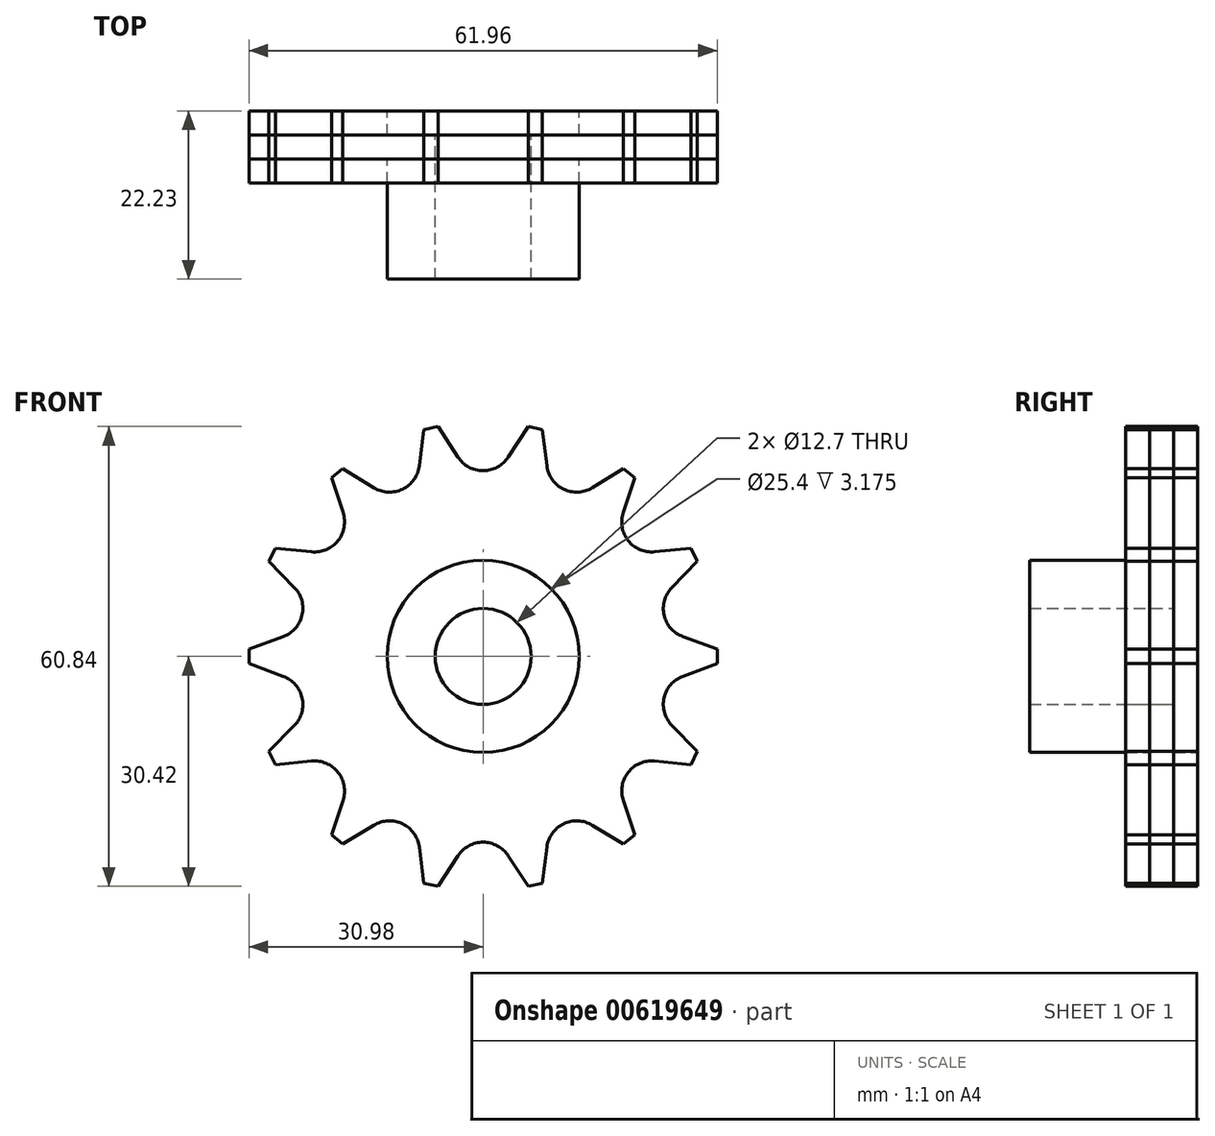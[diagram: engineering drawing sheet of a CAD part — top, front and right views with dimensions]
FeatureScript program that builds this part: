
annotation { "Feature Type Name" : "Feature", "Feature Type Description" : "" }
export const myFeature = defineFeature(function(context is Context, id is Id, definition is map)
    precondition{}
    {
        {
            var Q0;
            Q0=qCreatedBy(makeId("Front.planeOp"),FACE);
            var sketch = newSketch(context, id + "F0", { "sketchPlane" : qUnion([Q0])});
            skCircle(sketch, "E0", {"center": v(0, 0) * mm, "radius": 6.35 * mm});
            skCircle(sketch, "E1", {"center": v(0, 0) * mm, "radius": 12.7 * mm});
            skCircle(sketch, "E2", {"center": v(0, 0) * mm, "radius": 31.26 * mm, "construction": true});
            skLineSegment(sketch, "E3", {"start": v(0, 28.54) * mm, "end": v(0, 0) * mm, "construction": true});
            skLineSegment(sketch, "E4", {"start": v(0, 0) * mm, "end": v(38.17, 0) * mm, "construction": true});
            skLineSegment(sketch, "E5.1.0", {"start": v(-12.38, 25.71) * mm, "end": v(0, 0) * mm, "construction": true});
            skLineSegment(sketch, "E5.2.0", {"start": v(-22.31, 17.8) * mm, "end": v(0, 0) * mm, "construction": true});
            skLineSegment(sketch, "E5.3.0", {"start": v(-27.82, 6.35) * mm, "end": v(0, 0) * mm, "construction": true});
            skLineSegment(sketch, "E5.4.0", {"start": v(-27.82, -6.35) * mm, "end": v(0, 0) * mm, "construction": true});
            skLineSegment(sketch, "E5.5.0", {"start": v(-22.31, -17.8) * mm, "end": v(0, 0) * mm, "construction": true});
            skLineSegment(sketch, "E5.6.0", {"start": v(-12.38, -25.71) * mm, "end": v(0, 0) * mm, "construction": true});
            skLineSegment(sketch, "E5.7.0", {"start": v(0, -28.54) * mm, "end": v(0, 0) * mm, "construction": true});
            skLineSegment(sketch, "E5.8.0", {"start": v(12.38, -25.71) * mm, "end": v(0, 0) * mm, "construction": true});
            skLineSegment(sketch, "E5.9.0", {"start": v(22.31, -17.8) * mm, "end": v(0, 0) * mm, "construction": true});
            skLineSegment(sketch, "E5.10.0", {"start": v(27.82, -6.35) * mm, "end": v(0, 0) * mm, "construction": true});
            skLineSegment(sketch, "E5.11.0", {"start": v(27.82, 6.35) * mm, "end": v(0, 0) * mm, "construction": true});
            skLineSegment(sketch, "E5.12.0", {"start": v(22.31, 17.8) * mm, "end": v(0, 0) * mm, "construction": true});
            skLineSegment(sketch, "E5.13.0", {"start": v(12.38, 25.71) * mm, "end": v(0, 0) * mm, "construction": true});
            skCircle(sketch, "E6", {"center": v(0, 28.54) * mm, "radius": 3.97 * mm, "construction": true});
            skCircle(sketch, "E7.1.0", {"center": v(-12.38, 25.71) * mm, "radius": 3.97 * mm, "construction": true});
            skCircle(sketch, "E7.2.0", {"center": v(-22.31, 17.8) * mm, "radius": 3.97 * mm, "construction": true});
            skCircle(sketch, "E7.3.0", {"center": v(-27.82, 6.35) * mm, "radius": 3.97 * mm, "construction": true});
            skCircle(sketch, "E7.4.0", {"center": v(-27.82, -6.35) * mm, "radius": 3.97 * mm, "construction": true});
            skCircle(sketch, "E7.5.0", {"center": v(-22.31, -17.8) * mm, "radius": 3.97 * mm, "construction": true});
            skCircle(sketch, "E7.6.0", {"center": v(-12.38, -25.71) * mm, "radius": 3.97 * mm, "construction": true});
            skCircle(sketch, "E7.7.0", {"center": v(0, -28.54) * mm, "radius": 3.97 * mm, "construction": true});
            skCircle(sketch, "E7.8.0", {"center": v(12.38, -25.71) * mm, "radius": 3.97 * mm, "construction": true});
            skCircle(sketch, "E7.9.0", {"center": v(22.31, -17.8) * mm, "radius": 3.97 * mm, "construction": true});
            skCircle(sketch, "E7.10.0", {"center": v(27.82, -6.35) * mm, "radius": 3.97 * mm, "construction": true});
            skCircle(sketch, "E7.11.0", {"center": v(27.82, 6.35) * mm, "radius": 3.97 * mm, "construction": true});
            skCircle(sketch, "E7.12.0", {"center": v(22.31, 17.8) * mm, "radius": 3.97 * mm, "construction": true});
            skCircle(sketch, "E7.13.0", {"center": v(12.38, 25.71) * mm, "radius": 3.97 * mm, "construction": true});
            skLineSegment(sketch, "E8", {"start": v(0, 28.54) * mm, "end": v(12.38, 25.71) * mm, "construction": true});
            skLineSegment(sketch, "E9", {"start": v(0, 28.54) * mm, "end": v(-12.38, 25.71) * mm, "construction": true});
            skLineSegment(sketch, "E10", {"start": v(6.2, 27.12) * mm, "end": v(6.9, 30.2) * mm, "construction": true});
            skLineSegment(sketch, "E11", {"start": v(6.9, 30.2) * mm, "end": v(5.96, 30.42) * mm});
            skLineSegment(sketch, "E12", {"start": v(5.96, 30.42) * mm, "end": v(3.33, 26.37) * mm});
            skArc(sketch, "E13", {"start": v(0, 24.57) * mm, "mid": v(1.9, 25.05) * mm, "end": v(3.33, 26.37) * mm});
            skLineSegment(sketch, "E14.MirrorCS", {"start": v(6.9, 30.2) * mm, "end": v(7.83, 30) * mm});
            skLineSegment(sketch, "E15.MirrorCS", {"start": v(7.83, 30) * mm, "end": v(8.45, 25.2) * mm});
            skArc(sketch, "E16.MirrorCS", {"start": v(10.66, 22.13) * mm, "mid": v(9.16, 23.39) * mm, "end": v(8.45, 25.2) * mm});
            skArc(sketch, "E17.1.0", {"start": v(-10.66, 22.13) * mm, "mid": v(-9.16, 23.39) * mm, "end": v(-8.45, 25.2) * mm});
            skLineSegment(sketch, "E17.1.1", {"start": v(-7.83, 30) * mm, "end": v(-8.45, 25.2) * mm});
            skLineSegment(sketch, "E17.1.2", {"start": v(-6.9, 30.2) * mm, "end": v(-7.83, 30) * mm});
            skLineSegment(sketch, "E17.1.3", {"start": v(-6.9, 30.2) * mm, "end": v(-5.96, 30.42) * mm});
            skLineSegment(sketch, "E17.1.4", {"start": v(-5.96, 30.42) * mm, "end": v(-3.33, 26.37) * mm});
            skArc(sketch, "E17.1.5", {"start": v(0, 24.57) * mm, "mid": v(-1.9, 25.05) * mm, "end": v(-3.33, 26.37) * mm});
            skArc(sketch, "E17.2.0", {"start": v(-19.2, 15.32) * mm, "mid": v(-18.4, 17.1) * mm, "end": v(-18.54, 19.04) * mm});
            skLineSegment(sketch, "E17.2.1", {"start": v(-20.07, 23.63) * mm, "end": v(-18.54, 19.04) * mm});
            skLineSegment(sketch, "E17.2.2", {"start": v(-19.32, 24.22) * mm, "end": v(-20.07, 23.63) * mm});
            skLineSegment(sketch, "E17.2.3", {"start": v(-19.32, 24.22) * mm, "end": v(-18.57, 24.82) * mm});
            skLineSegment(sketch, "E17.2.4", {"start": v(-18.57, 24.82) * mm, "end": v(-14.44, 22.32) * mm});
            skArc(sketch, "E17.2.5", {"start": v(-10.66, 22.13) * mm, "mid": v(-12.57, 21.75) * mm, "end": v(-14.44, 22.32) * mm});
            skArc(sketch, "E17.3.0", {"start": v(-23.95, 5.47) * mm, "mid": v(-24, 7.42) * mm, "end": v(-24.97, 9.1) * mm});
            skLineSegment(sketch, "E17.3.1", {"start": v(-28.33, 12.58) * mm, "end": v(-24.97, 9.1) * mm});
            skLineSegment(sketch, "E17.3.2", {"start": v(-27.92, 13.44) * mm, "end": v(-28.33, 12.58) * mm});
            skLineSegment(sketch, "E17.3.3", {"start": v(-27.92, 13.44) * mm, "end": v(-27.5, 14.3) * mm});
            skLineSegment(sketch, "E17.3.4", {"start": v(-27.5, 14.3) * mm, "end": v(-22.7, 13.84) * mm});
            skArc(sketch, "E17.3.5", {"start": v(-19.2, 15.32) * mm, "mid": v(-20.76, 14.14) * mm, "end": v(-22.7, 13.84) * mm});
            skArc(sketch, "E17.4.0", {"start": v(-23.95, -5.47) * mm, "mid": v(-24.84, -3.73) * mm, "end": v(-26.45, -2.63) * mm});
            skLineSegment(sketch, "E17.4.1", {"start": v(-30.98, -0.96) * mm, "end": v(-26.45, -2.63) * mm});
            skLineSegment(sketch, "E17.4.2", {"start": v(-30.98, 0) * mm, "end": v(-30.98, -0.96) * mm});
            skLineSegment(sketch, "E17.4.3", {"start": v(-30.98, 0) * mm, "end": v(-30.98, 0.96) * mm});
            skLineSegment(sketch, "E17.4.4", {"start": v(-30.98, 0.96) * mm, "end": v(-26.45, 2.63) * mm});
            skArc(sketch, "E17.4.5", {"start": v(-23.95, 5.47) * mm, "mid": v(-24.84, 3.73) * mm, "end": v(-26.45, 2.63) * mm});
            skArc(sketch, "E17.5.0", {"start": v(-19.2, -15.32) * mm, "mid": v(-20.76, -14.14) * mm, "end": v(-22.7, -13.84) * mm});
            skLineSegment(sketch, "E17.5.1", {"start": v(-27.5, -14.3) * mm, "end": v(-22.7, -13.84) * mm});
            skLineSegment(sketch, "E17.5.2", {"start": v(-27.92, -13.44) * mm, "end": v(-27.5, -14.3) * mm});
            skLineSegment(sketch, "E17.5.3", {"start": v(-27.92, -13.44) * mm, "end": v(-28.33, -12.58) * mm});
            skLineSegment(sketch, "E17.5.4", {"start": v(-28.33, -12.58) * mm, "end": v(-24.97, -9.1) * mm});
            skArc(sketch, "E17.5.5", {"start": v(-23.95, -5.47) * mm, "mid": v(-24, -7.42) * mm, "end": v(-24.97, -9.1) * mm});
            skArc(sketch, "E17.6.0", {"start": v(-10.66, -22.13) * mm, "mid": v(-12.57, -21.75) * mm, "end": v(-14.44, -22.32) * mm});
            skLineSegment(sketch, "E17.6.1", {"start": v(-18.57, -24.82) * mm, "end": v(-14.44, -22.32) * mm});
            skLineSegment(sketch, "E17.6.2", {"start": v(-19.32, -24.22) * mm, "end": v(-18.57, -24.82) * mm});
            skLineSegment(sketch, "E17.6.3", {"start": v(-19.32, -24.22) * mm, "end": v(-20.07, -23.63) * mm});
            skLineSegment(sketch, "E17.6.4", {"start": v(-20.07, -23.63) * mm, "end": v(-18.54, -19.04) * mm});
            skArc(sketch, "E17.6.5", {"start": v(-19.2, -15.32) * mm, "mid": v(-18.4, -17.1) * mm, "end": v(-18.54, -19.04) * mm});
            skArc(sketch, "E17.7.0", {"start": v(0, -24.57) * mm, "mid": v(-1.9, -25.05) * mm, "end": v(-3.33, -26.37) * mm});
            skLineSegment(sketch, "E17.7.1", {"start": v(-5.96, -30.42) * mm, "end": v(-3.33, -26.37) * mm});
            skLineSegment(sketch, "E17.7.2", {"start": v(-6.9, -30.2) * mm, "end": v(-5.96, -30.42) * mm});
            skLineSegment(sketch, "E17.7.3", {"start": v(-6.9, -30.2) * mm, "end": v(-7.83, -30) * mm});
            skLineSegment(sketch, "E17.7.4", {"start": v(-7.83, -30) * mm, "end": v(-8.45, -25.2) * mm});
            skArc(sketch, "E17.7.5", {"start": v(-10.66, -22.13) * mm, "mid": v(-9.16, -23.39) * mm, "end": v(-8.45, -25.2) * mm});
            skArc(sketch, "E17.8.0", {"start": v(10.66, -22.13) * mm, "mid": v(9.16, -23.39) * mm, "end": v(8.45, -25.2) * mm});
            skLineSegment(sketch, "E17.8.1", {"start": v(7.83, -30) * mm, "end": v(8.45, -25.2) * mm});
            skLineSegment(sketch, "E17.8.2", {"start": v(6.9, -30.2) * mm, "end": v(7.83, -30) * mm});
            skLineSegment(sketch, "E17.8.3", {"start": v(6.9, -30.2) * mm, "end": v(5.96, -30.42) * mm});
            skLineSegment(sketch, "E17.8.4", {"start": v(5.96, -30.42) * mm, "end": v(3.33, -26.37) * mm});
            skArc(sketch, "E17.8.5", {"start": v(0, -24.57) * mm, "mid": v(1.9, -25.05) * mm, "end": v(3.33, -26.37) * mm});
            skArc(sketch, "E17.9.0", {"start": v(19.2, -15.32) * mm, "mid": v(18.4, -17.1) * mm, "end": v(18.54, -19.04) * mm});
            skLineSegment(sketch, "E17.9.1", {"start": v(20.07, -23.63) * mm, "end": v(18.54, -19.04) * mm});
            skLineSegment(sketch, "E17.9.2", {"start": v(19.32, -24.22) * mm, "end": v(20.07, -23.63) * mm});
            skLineSegment(sketch, "E17.9.3", {"start": v(19.32, -24.22) * mm, "end": v(18.57, -24.82) * mm});
            skLineSegment(sketch, "E17.9.4", {"start": v(18.57, -24.82) * mm, "end": v(14.44, -22.32) * mm});
            skArc(sketch, "E17.9.5", {"start": v(10.66, -22.13) * mm, "mid": v(12.57, -21.75) * mm, "end": v(14.44, -22.32) * mm});
            skArc(sketch, "E17.10.0", {"start": v(23.95, -5.47) * mm, "mid": v(24, -7.42) * mm, "end": v(24.97, -9.1) * mm});
            skLineSegment(sketch, "E17.10.1", {"start": v(28.33, -12.58) * mm, "end": v(24.97, -9.1) * mm});
            skLineSegment(sketch, "E17.10.2", {"start": v(27.92, -13.44) * mm, "end": v(28.33, -12.58) * mm});
            skLineSegment(sketch, "E17.10.3", {"start": v(27.92, -13.44) * mm, "end": v(27.5, -14.3) * mm});
            skLineSegment(sketch, "E17.10.4", {"start": v(27.5, -14.3) * mm, "end": v(22.7, -13.84) * mm});
            skArc(sketch, "E17.10.5", {"start": v(19.2, -15.32) * mm, "mid": v(20.76, -14.14) * mm, "end": v(22.7, -13.84) * mm});
            skArc(sketch, "E17.11.0", {"start": v(23.95, 5.47) * mm, "mid": v(24.84, 3.73) * mm, "end": v(26.45, 2.63) * mm});
            skLineSegment(sketch, "E17.11.1", {"start": v(30.98, 0.96) * mm, "end": v(26.45, 2.63) * mm});
            skLineSegment(sketch, "E17.11.2", {"start": v(30.98, 0) * mm, "end": v(30.98, 0.96) * mm});
            skLineSegment(sketch, "E17.11.3", {"start": v(30.98, 0) * mm, "end": v(30.98, -0.96) * mm});
            skLineSegment(sketch, "E17.11.4", {"start": v(30.98, -0.96) * mm, "end": v(26.45, -2.63) * mm});
            skArc(sketch, "E17.11.5", {"start": v(23.95, -5.47) * mm, "mid": v(24.84, -3.73) * mm, "end": v(26.45, -2.63) * mm});
            skArc(sketch, "E17.12.0", {"start": v(19.2, 15.32) * mm, "mid": v(20.76, 14.14) * mm, "end": v(22.7, 13.84) * mm});
            skLineSegment(sketch, "E17.12.1", {"start": v(27.5, 14.3) * mm, "end": v(22.7, 13.84) * mm});
            skLineSegment(sketch, "E17.12.2", {"start": v(27.92, 13.44) * mm, "end": v(27.5, 14.3) * mm});
            skLineSegment(sketch, "E17.12.3", {"start": v(27.92, 13.44) * mm, "end": v(28.33, 12.58) * mm});
            skLineSegment(sketch, "E17.12.4", {"start": v(28.33, 12.58) * mm, "end": v(24.97, 9.1) * mm});
            skArc(sketch, "E17.12.5", {"start": v(23.95, 5.47) * mm, "mid": v(24, 7.42) * mm, "end": v(24.97, 9.1) * mm});
            skArc(sketch, "E17.13.0", {"start": v(10.66, 22.13) * mm, "mid": v(12.57, 21.75) * mm, "end": v(14.44, 22.32) * mm});
            skLineSegment(sketch, "E17.13.1", {"start": v(18.57, 24.82) * mm, "end": v(14.44, 22.32) * mm});
            skLineSegment(sketch, "E17.13.2", {"start": v(19.32, 24.22) * mm, "end": v(18.57, 24.82) * mm});
            skLineSegment(sketch, "E17.13.3", {"start": v(19.32, 24.22) * mm, "end": v(20.07, 23.63) * mm});
            skLineSegment(sketch, "E17.13.4", {"start": v(20.07, 23.63) * mm, "end": v(18.54, 19.04) * mm});
            skArc(sketch, "E17.13.5", {"start": v(19.2, 15.32) * mm, "mid": v(18.4, 17.1) * mm, "end": v(18.54, 19.04) * mm});
            skSolve(sketch);
        }
        {
            var Q0;
            Q0=makeQuery(id+"F0.imprint","IMPRINT",FACE,{"disambiguationData":[TD([[makeQuery(id+"F0.imprint","IMPRINT",EDGE,{"derivedFrom":sQuery(id+"F0.wireOp",EDGE,"E1")}),-1.0]])]});
            extrude(context, id + "F1", {"entities" : qUnion([Q0]), "endBound" : BoundingType.SYMMETRIC, "depth" : 6.35 * mm, "offsetDistance" : 25.4 * mm});
        }
        {
            var Q0;
            Q0=makeQuery(id+"F0.imprint","IMPRINT",FACE,{"disambiguationData":[TD([[makeQuery(id+"F0.imprint","IMPRINT",EDGE,{"derivedFrom":sQuery(id+"F0.wireOp",EDGE,"E0")}),-1.0]])]});
            extrude(context, id + "F2", {"entities" : qUnion([Q0]), "operationType" : NewBodyOperationType.ADD, "depth" : 19.05 * mm, "offsetDistance" : 25.4 * mm});
        }
        {
            var Q0;
            Q0=makeQuery(id+"F0.imprint","IMPRINT",FACE,{"disambiguationData":[TD([[makeQuery(id+"F0.imprint","IMPRINT",EDGE,{"derivedFrom":sQuery(id+"F0.wireOp",EDGE,"E0")}),-1.0]])]});
            var Q1;
            Q1=makeQuery(id+"F0.imprint","IMPRINT",FACE,{"disambiguationData":[TD([[makeQuery(id+"F0.imprint","IMPRINT",EDGE,{"derivedFrom":sQuery(id+"F0.wireOp",EDGE,"E1")}),-1.0]])]});
            extrude(context, id + "F3", {"entities" : qUnion([Q0, Q1]), "depth" : 6.35 * mm, "offsetDistance" : 25.4 * mm});
        }
    });
